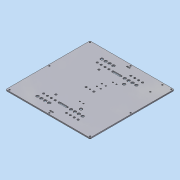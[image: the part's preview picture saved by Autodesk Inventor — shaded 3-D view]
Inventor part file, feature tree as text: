
AUTODESK INVENTOR PART (.ipt)
format: ipt  version: 2013 (Build 170138000, 138)  size: 269,824 bytes
history: native  units: mm
features: sketch x13, hole x10, extrude x3, mirror x2, fillet x1
ambient origin geometry x8: Origin, YZ Plane, XZ Plane, XY Plane, X Axis, Y Axis, Z Axis, Center Point
bodies: Solid1 (feature_tree)
feature tree (29):
  extrude  "Extrusion1"  Depth=216.0mm
  hole  "Hole1"  [1 undecoded]
  hole  "Hole2"  [1 undecoded]
  hole  "Hole3"  [1 undecoded]
  hole  "Hole4"  [1 undecoded]
  hole  "Hole5"  [1 undecoded]
  mirror  "Mirror1"
  hole  "Hole6"  [1 undecoded]
  hole  "Hole7"  [1 undecoded]
  hole  "Hole8"  [1 undecoded]
  hole  "Hole9"  [1 undecoded]
  extrude  "Extrusion2"  Depth=55.35mm
  extrude  "Extrusion3"  Depth=75.7mm
  mirror  "Mirror2"
  hole  "Hole10"  [1 undecoded]
  fillet  "Fillet1"  Radius=10.0mm
  sketch  "Sketch1"  dims[d0=216.0mm d2=216.0mm]
  sketch  "Sketch2"  dims[d3=3.0mm d4=0.0mm d5=3.5mm]
  sketch  "Sketch3"  dims[d6=3.6mm d7=1.7mm]
  sketch  "Sketch4"  dims[d8=3.5mm d9=3.5mm]
  sketch  "Sketch5"  dims[d10=3.5mm d11=3.5mm]
  sketch  "Sketch6"  dims[d13=108.0mm]
  sketch  "Sketch7"  dims[d14=3.6mm d15=6.0mm d16=4.0mm d17=2.0mm d18=90.0deg d19=8.0mm d20=20.594885mm d21=25.35mm]
  sketch  "Sketch8"  dims[d23=39.0mm d24=160.3mm]
  sketch  "Sketch9"  dims[d25=150.3mm d26=140.3mm]
  sketch  "Sketch10"  dims[d27=130.3mm d28=57.68mm]
  sketch  "Sketch11"  dims[d29=67.68mm d30=77.68mm]
  sketch  "Sketch12"  dims[d31=87.68mm]
  sketch  "Sketch13"  dims[d32=7.14mm d33=6.0mm d34=4.0mm d35=2.0mm d36=90.0deg d37=8.0mm d38=20.594885mm d39=5.0mm d40=6.0mm d41=4.0mm d42=2.0mm d43=90.0deg d44=8.0mm d45=20.594885mm d46=55.35mm d47=75.7mm d48=5.0mm d49=6.0mm d50=4.0mm d51=2.0mm d52=90.0deg d53=8.0mm d54=20.594885mm d55=64.6mm d56=7.14mm d57=6.0mm d58=4.0mm d59=2.0mm d60=90.0deg d61=8.0mm d62=20.594885mm d63=10.0mm d64=10.0mm d65=5.0mm d66=6.0mm d67=4.0mm d68=2.0mm d69=90.0deg d70=8.0mm d71=20.594885mm d72=80.0mm d73=10.14mm d74=12.83mm d75=110.5mm d76=3.5mm d77=6.0mm d78=4.0mm d79=2.0mm d80=90.0deg d81=8.0mm d82=20.594885mm d83=122.0mm d84=63.0mm d85=9.12mm d86=3.14mm d87=6.0mm d88=4.0mm d89=2.0mm d90=90.0deg d91=8.0mm d92=20.594885mm d93=68.0mm d94=9.12mm d95=3.14mm d96=6.0mm d97=4.0mm d98=2.0mm d99=90.0deg d100=8.0mm d101=20.594885mm d104=9.38mm d105=6.5mm d106=3.0mm d107=4.0mm d108=0.0mm d109=5.0mm d111=39.0mm d112=20.0mm d113=4.0mm d114=0.0mm d115=1.58mm d116=21.5mm d117=36.0mm d118=3.6mm d119=6.0mm d120=4.0mm d121=2.0mm d122=90.0deg d123=8.0mm d124=20.594885mm d125=158.32mm d126=148.32mm d127=138.32mm d128=128.32mm d129=55.7mm d130=65.7mm d131=75.7mm d132=85.7mm d133=1.75mm]
note: 10 required parameter values undecoded (feature->parameter linkage not recoverable at this tier; creation-order binding heuristic only, values carry confidence <= 0.55)
